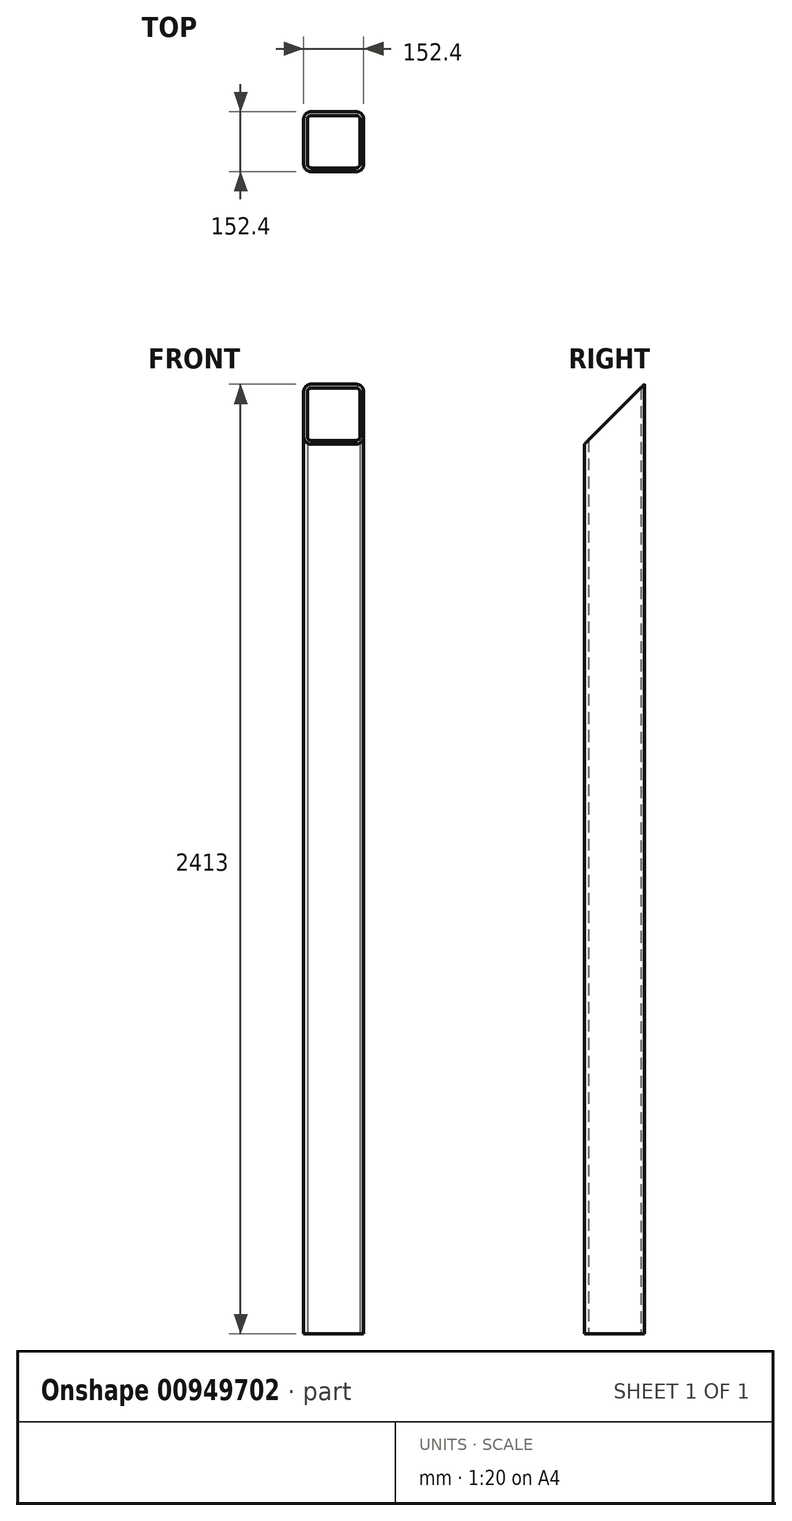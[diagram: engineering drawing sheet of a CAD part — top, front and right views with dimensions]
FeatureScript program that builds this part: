
annotation { "Feature Type Name" : "Feature", "Feature Type Description" : "" }
export const myFeature = defineFeature(function(context is Context, id is Id, definition is map)
    precondition{}
    {
        {
            var Q0;
            Q0=qCreatedBy(makeId("Top.planeOp"),FACE);
            var sketch = newSketch(context, id + "F0", { "sketchPlane" : qUnion([Q0])});
            skLineSegment(sketch, "E0.bottom", {"start": v(-57.15, -76.2) * mm, "end": v(57.15, -76.2) * mm});
            skLineSegment(sketch, "E0.top", {"start": v(-57.15, 76.2) * mm, "end": v(57.15, 76.2) * mm});
            skLineSegment(sketch, "E0.left", {"start": v(-76.2, -57.15) * mm, "end": v(-76.2, 57.15) * mm});
            skLineSegment(sketch, "E0.right", {"start": v(76.2, -57.15) * mm, "end": v(76.2, 57.15) * mm});
            skPoint(sketch, "E0.middle", {"position": v(0, 0) * mm});
            skLineSegment(sketch, "E1.bottom", {"start": v(-57.15, -66.68) * mm, "end": v(57.15, -66.68) * mm});
            skLineSegment(sketch, "E1.top", {"start": v(-57.15, 66.68) * mm, "end": v(57.15, 66.68) * mm});
            skLineSegment(sketch, "E1.left", {"start": v(-66.68, -57.15) * mm, "end": v(-66.68, 57.15) * mm});
            skLineSegment(sketch, "E1.right", {"start": v(66.68, -57.15) * mm, "end": v(66.68, 57.15) * mm});
            skPoint(sketch, "E2.visualSharp", {"position": v(-76.2, 76.2) * mm});
            skArc(sketch, "E2.filletArc", {"start": v(-57.15, 76.2) * mm, "mid": v(-70.62, 70.62) * mm, "end": v(-76.2, 57.15) * mm});
            skPoint(sketch, "E3.visualSharp", {"position": v(-76.2, -76.2) * mm});
            skArc(sketch, "E3.filletArc", {"start": v(-76.2, -57.15) * mm, "mid": v(-70.62, -70.62) * mm, "end": v(-57.15, -76.2) * mm});
            skPoint(sketch, "E4.visualSharp", {"position": v(76.2, -76.2) * mm});
            skArc(sketch, "E4.filletArc", {"start": v(57.15, -76.2) * mm, "mid": v(70.62, -70.62) * mm, "end": v(76.2, -57.15) * mm});
            skPoint(sketch, "E5.visualSharp", {"position": v(76.2, 76.2) * mm});
            skArc(sketch, "E5.filletArc", {"start": v(76.2, 57.15) * mm, "mid": v(70.62, 70.62) * mm, "end": v(57.15, 76.2) * mm});
            skPoint(sketch, "E6.visualSharp", {"position": v(-66.68, 66.68) * mm});
            skArc(sketch, "E6.filletArc", {"start": v(-57.15, 66.68) * mm, "mid": v(-63.89, 63.89) * mm, "end": v(-66.68, 57.15) * mm});
            skPoint(sketch, "E7.visualSharp", {"position": v(-66.68, -66.68) * mm});
            skArc(sketch, "E7.filletArc", {"start": v(-66.68, -57.15) * mm, "mid": v(-63.89, -63.89) * mm, "end": v(-57.15, -66.68) * mm});
            skPoint(sketch, "E8.visualSharp", {"position": v(66.68, -66.68) * mm});
            skArc(sketch, "E8.filletArc", {"start": v(57.15, -66.68) * mm, "mid": v(63.89, -63.89) * mm, "end": v(66.68, -57.15) * mm});
            skPoint(sketch, "E9.visualSharp", {"position": v(66.68, 66.68) * mm});
            skArc(sketch, "E9.filletArc", {"start": v(66.68, 57.15) * mm, "mid": v(63.89, 63.89) * mm, "end": v(57.15, 66.68) * mm});
            skSolve(sketch);
        }
        {
            var Q0;
            Q0=qSketchRegion(id+"F0",true);
            extrude(context, id + "F1", {"entities" : qUnion([Q0]), "depth" : 2413 * mm, "offsetDistance" : 25.4 * mm});
        }
        {
            var Q0;
            Q0=qCreatedBy(makeId("Right.planeOp"),FACE);
            var sketch = newSketch(context, id + "F2", { "sketchPlane" : qUnion([Q0])});
            skLineSegment(sketch, "E10", {"start": v(-76.2, 2413) * mm, "end": v(76.2, 2413) * mm});
            skLineSegment(sketch, "E11", {"start": v(76.2, 2413) * mm, "end": v(-76.2, 2260.6) * mm});
            skLineSegment(sketch, "E12", {"start": v(-76.2, 2260.6) * mm, "end": v(-76.2, 2413) * mm});
            skSolve(sketch);
        }
        {
            var Q0;
            Q0=qSketchRegion(id+"F2",true);
            extrude(context, id + "F3", {"entities" : qUnion([Q0]), "operationType" : NewBodyOperationType.REMOVE, "endBound" : BoundingType.THROUGH_ALL, "oppositeDirection" : true, "depth" : 25.4 * mm, "offsetDistance" : 25.4 * mm, "hasSecondDirection" : true, "secondDirectionBound" : SecondDirectionBoundingType.THROUGH_ALL, "secondDirectionOppositeDirection" : false, "secondDirectionDepth" : 25.4 * mm});
        }
    });
